# Revit family: QF_BOURGEAT_Self_Bain_marie_air_6GN
name_source: partatom
category: Equipement spécialisé
revit_build: Autodesk Revit 2015 (Build: 20140606_1530(x64)
units: mm (PartAtom-declared; Revit-internal decimal feet)

## types (17) — shared parameters
Certification = NF alimentaire
Charge max = 200.00 kg
Cuve à air = Oui
Cuve à eau = Non
Fabricant = BOURGEAT
Fréquence = 50 Hz
Indice de protection = 21
Longueur hors tout = 2184 mm  [stored 7.16535 ft]
Nature isolant = Laine de verre
Phase = 2
Profondeur hors tout = 820 mm  [stored 2.69029 ft]
Spécification du Fabricant = Bain-marie Oasis
Tension = 230 V
URL Fabricant = http://www.bourgeat.fr
lg_etagere = 1712 mm  [stored 5.6168 ft]
lg_porte = 866 mm
lg_presentoir = 2072 mm  [stored 6.7979 ft]
lgconsole = 2140 mm  [stored 7.021 ft]
lgmeuble = 2116 mm  [stored 6.94226 ft]

## per-type parameters (varying)
| type | Etageres | Hauteur hors tout | Intensité nominale | Modèle | Pieds | Poids net à vide | Presentoir | Puissance électrique  | Reserves | Roues |
| 6GN_Baie_libre+presentoir_chauffant+roue+etageres | Oui | 1330 mm | 25 A | 851016+851306+854950+854936 | Non | 240.00 kg | Oui | 5860 W | Non | Oui |
| 6GN_baie_libre | Non | 900 mm | 21 A | 851016 | Oui | 210.00 kg | Non | 4900 W | Non | Non |
| 6GN_baie_libre+roues | Non | 900 mm | 21 A | 851016+854950 | Non | 210.00 kg | Non | 4900 W | Non | Oui |
| 6GN_baie_libre+etageres | Oui | 900 mm | 21 A | 851016+854933 | Oui | 210.00 kg | Non | 4900 W | Non | Non |
| 6GN_baie_libre+presentoir_neutre | Non | 1330 mm | 21 A | 851016+851316 | Oui | 240.00 kg | Oui | 4900 W | Non | Non |
| 6GN_baie_libre+roues+etageres | Oui | 900 mm | 21 A | 851016+854950+851306 | Non | 210.00 kg | Non | 4900 W | Non | Oui |
| 6GN_baie_libre+roues+presentoir_neutre | Non | 1330 mm | 21 A | 851016+854950+851316 | Non | 240.00 kg | Oui | 4900 W | Non | Oui |
| 6GN_baie_libre+roues+presentoir_chauffant | Non | 1330 mm | 25 A | 851016+854950+851306 | Non | 240.00 kg | Oui | 5860 W | Non | Oui |
| 6GN_baie_libre+etageres+presentoir_neutre | Oui | 1330 mm | 21 A | 851016+854933+851316 | Oui | 240.00 kg | Oui | 4900 W | Non | Non |
| 6GN_baie_libre+etageres+presentoir_chauffant | Oui | 1330 mm | 21 A | 851016+854933+851306 | Oui | 240.00 kg | Oui | 4900 W | Non | Non |
| 6GN_Baie_libre+presentoir_neutre+roue+etageres | Oui | 1330 mm | 25 A | 851016+851316+854950+854936 | Non | 240.00 kg | Oui | 5860 W | Non | Oui |
| 6GN_reserve | Non | 900 mm | 25 A | 851216 | Oui | 210.00 kg | Non | 5800 W | Oui | Non |
| 6GN_reserve+roues | Non | 900 mm | 25 A | 851216+854950 | Non | 210.00 kg | Non | 5800 W | Oui | Oui |
| 6GN_reserve+presentoir_neutre | Non | 1330 mm | 25 A | 851216+851316 | Oui | 240.00 kg | Oui | 5800 W | Oui | Non |
| 6GN_reserve+presentoir_chauffant | Non | 1330 mm | 29 A | 851216+851306 | Oui | 240.00 kg | Oui | 6760 W | Oui | Non |
| 6GN_reserve+presentoir_chauffant+roues | Non | 1330 mm | 29 A | 851216+851306+854950 | Non | 240.00 kg | Oui | 6760 W | Oui | Oui |
| 6GN_reserve+presentoir_neutre+roues | Non | 1330 mm | 25 A | 851216+851316+854950 | Non | 240.00 kg | Oui | 5800 W | Oui | Oui |

note: [stored X ft] marks values corroborated as IEEE doubles in the binary element streams (Revit-internal decimal feet)

## geometry (parser evidence)
native form markers: Blend x12
no freeform markers — native parametric forms only
